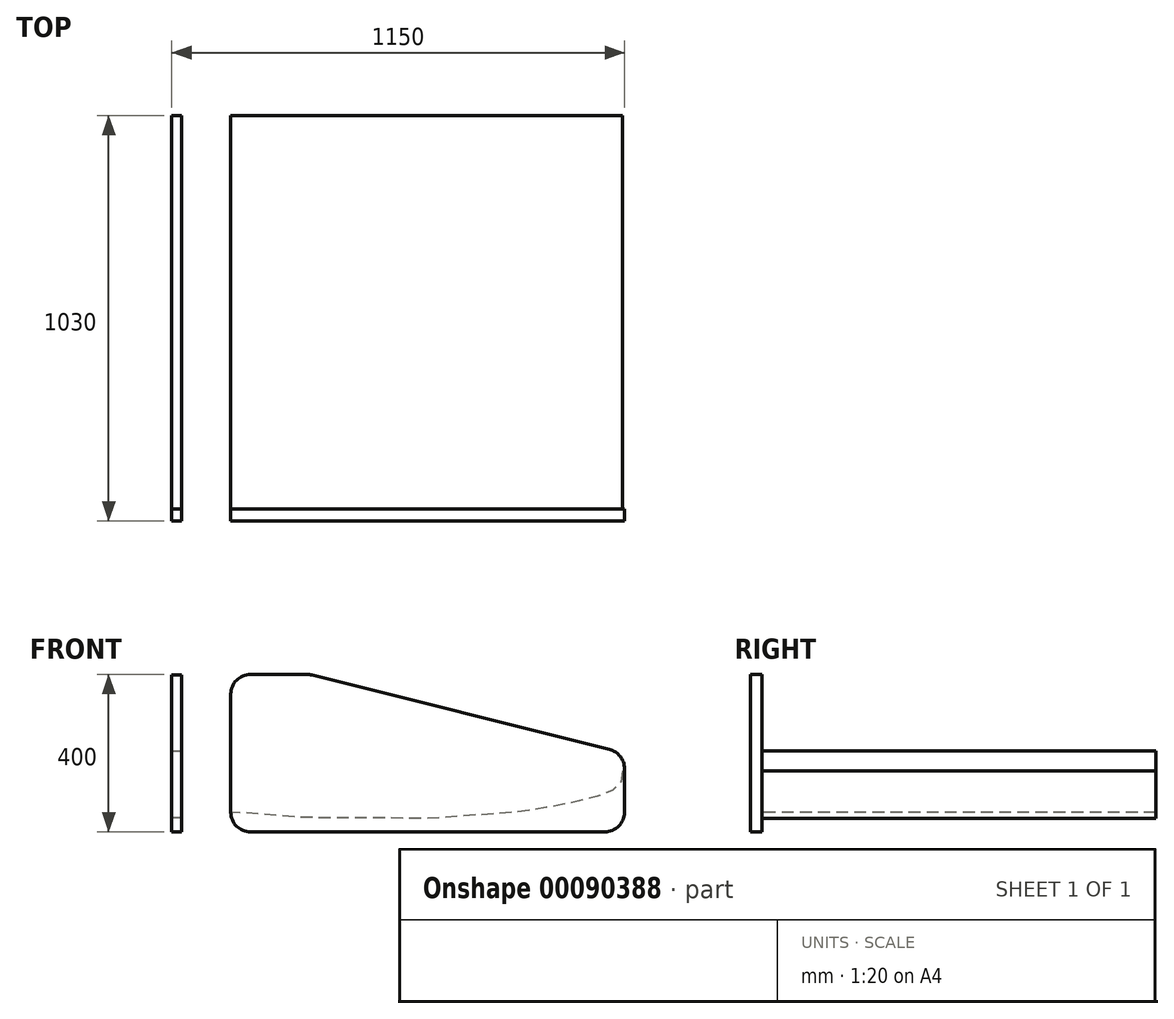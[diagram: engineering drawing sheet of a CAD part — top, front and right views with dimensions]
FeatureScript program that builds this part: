
annotation { "Feature Type Name" : "Feature", "Feature Type Description" : "" }
export const myFeature = defineFeature(function(context is Context, id is Id, definition is map)
    precondition{}
    {
        {
            var Q0;
            Q0=qCreatedBy(makeId("Front.planeOp"),FACE);
            var sketch = newSketch(context, id + "F0", { "sketchPlane" : qUnion([Q0])});
            skFitSpline(sketch, "E0", {"points": [v(500, -115.65) * mm, v(486.98, -151.94) * mm, v(400.8, -177.57) * mm, v(301.65, -187.35) * mm, v(199.93, -190.98) * mm, v(100.11, -187.23) * mm, v(-0.38, -183.55) * mm, v(-133.74, -168.4) * mm, v(-300.9, -150.5) * mm, v(-433.38, -126.44) * mm, v(-500, -115.65) * mm]});
            skFitSpline(sketch, "E1", {"points": [v(500, -115.65) * mm, v(486.98, -79.36) * mm, v(400.8, -53.72) * mm, v(301.65, -43.94) * mm, v(199.93, -40.32) * mm, v(100.11, -44.06) * mm, v(-0.38, -47.75) * mm, v(-133.74, -62.9) * mm, v(-300.9, -80.8) * mm, v(-433.38, -104.86) * mm, v(-500, -115.65) * mm]});
            skLineSegment(sketch, "E2", {"start": v(-500, -115.65) * mm, "end": v(0, 0) * mm, "construction": true});
            skSolve(sketch);
        }
        {
            var Q0;
            Q0 = qSketchRegion(id + "F0", true);
            extrude(context, id + "F1", {"entities" : qUnion([Q0]), "oppositeDirection" : true, "depth" : 1000 * mm});
        }
        {
            var Q0;
            Q0=makeQuery(id+"F1.opExtrude","SWEPT_BODY",BODY,{"disambiguationData":[OSD([sQuery(id+"F0.wireOp",EDGE,"E0"),sQuery(id+"F0.wireOp",EDGE,"E1")])]});
            var Q1;
            Q1=sQuery(id+"F0.wireOp",EDGE,"E2");
            transform(context, id + "F2", {"entities" : qUnion([Q0]), "transformType" : TransformType.TRANSLATION_ENTITY, "oppositeDirectionEntity" : false, "transformLine" : qUnion([Q1]), "makeCopy" : false});
        }
        {
            var Q0;
            Q0=makeQuery(id+"F1.opExtrude","SWEPT_BODY",BODY,{"disambiguationData":[OSD([sQuery(id+"F0.wireOp",EDGE,"E0"),sQuery(id+"F0.wireOp",EDGE,"E1")])]});
            var Q1;
            {var subQ0=sQuery(id+"F0.wireOp",EDGE,"E1");var subQ1=sQuery(id+"F0.wireOp",EDGE,"E0");Q1=makeQuery(id+"F1.opExtrude","SWEPT_EDGE",EDGE,{"disambiguationData":[OSD([subQ1,subQ0]),TDD([makeQuery(id+"F0.imprint","INTERSECT",VERTEX,{"disambiguationData":[OD(1.0)],"derivedFrom":[subQ1,subQ0]})])]});}
            transform(context, id + "F3", {"entities" : qUnion([Q0]), "transformType" : TransformType.ROTATION, "transformAxis" : qUnion([Q1]), "angle" : 6 * degree, "makeCopy" : false});
        }
        {
            var Q0;
            Q0=qCreatedBy(makeId("Front.planeOp"),FACE);
            var sketch = newSketch(context, id + "F4", { "sketchPlane" : qUnion([Q0])});
            skLineSegment(sketch, "E3", {"start": v(0, -50) * mm, "end": v(0, 350) * mm});
            skLineSegment(sketch, "E4", {"start": v(0, 350) * mm, "end": v(200, 350) * mm});
            skLineSegment(sketch, "E5", {"start": v(200, 350) * mm, "end": v(1000, 150) * mm});
            skLineSegment(sketch, "E6", {"start": v(1000, 150) * mm, "end": v(1000, -50) * mm});
            skLineSegment(sketch, "E7", {"start": v(1000, -50) * mm, "end": v(0, -50) * mm});
            skSolve(sketch);
        }
        {
            var Q0;
            Q0 = qSketchRegion(id + "F4", true);
            extrude(context, id + "F5", {"entities" : qUnion([Q0]), "operationType" : NewBodyOperationType.ADD, "depth" : 30 * mm});
        }
        {
            var Q0;
            Q0=makeQuery(id+"F5.opExtrude","SWEPT_EDGE",EDGE,{"disambiguationData":[OSD([sQuery(id+"F4.wireOp",EDGE,"E3"),sQuery(id+"F4.wireOp",EDGE,"E4")])]});
            var Q1;
            Q1=makeQuery(id+"F5.opExtrude","SWEPT_EDGE",EDGE,{"disambiguationData":[OSD([sQuery(id+"F4.wireOp",EDGE,"E4"),sQuery(id+"F4.wireOp",EDGE,"E5")])]});
            var Q2;
            Q2=makeQuery(id+"F5.opExtrude","SWEPT_EDGE",EDGE,{"disambiguationData":[OSD([sQuery(id+"F4.wireOp",EDGE,"E5"),sQuery(id+"F4.wireOp",EDGE,"E6")])]});
            var Q3;
            Q3=makeQuery(id+"F5.opExtrude","SWEPT_EDGE",EDGE,{"disambiguationData":[OSD([sQuery(id+"F4.wireOp",EDGE,"E6"),sQuery(id+"F4.wireOp",EDGE,"E7")])]});
            var Q4;
            Q4=makeQuery(id+"F5.opExtrude","SWEPT_EDGE",EDGE,{"disambiguationData":[OSD([sQuery(id+"F4.wireOp",EDGE,"E3"),sQuery(id+"F4.wireOp",EDGE,"E7")])]});
            fillet(context, id + "F6", {"entities" : qUnion([Q0, Q1, Q2, Q3, Q4]), "radius" : 50 * mm, "tangentPropagation" : true, "allowEdgeOverflow" : false});
        }
        {
            var Q0;
            Q0=qCreatedBy(makeId("Right.planeOp"),FACE);
            cPlane(context, id + "F7", {"entities" : qUnion([Q0]), "cplaneType" : CPlaneType.OFFSET, "offset" : 150 * mm, "oppositeDirection" : true, "width" : 150 * mm, "height" : 150 * mm});
        }
        {
            var Q0;
            Q0=qCreatedBy(id+"F7.planeOp",FACE);
            var sketch = newSketch(context, id + "F8", { "sketchPlane" : qUnion([Q0])});
            skLineSegment(sketch, "E8.0", {"start": v(-30, 348.5) * mm, "end": v(-30, 159.47) * mm});
            skLineSegment(sketch, "E9.0", {"start": v(0, 348.5) * mm, "end": v(-30, 348.5) * mm});
            skLineSegment(sketch, "E10.0", {"start": v(0, 348.5) * mm, "end": v(0, 159.47) * mm});
            skLineSegment(sketch, "E11", {"start": v(0, 154.88) * mm, "end": v(1000, 154.88) * mm});
            skLineSegment(sketch, "E12.0", {"start": v(-30, 110.96) * mm, "end": v(-30, 159.47) * mm});
            skLineSegment(sketch, "E13.0", {"start": v(-30, 110.96) * mm, "end": v(-30, 0) * mm});
            skLineSegment(sketch, "E14.0", {"start": v(-30, -50) * mm, "end": v(-30, 0) * mm});
            skLineSegment(sketch, "E15.0", {"start": v(0, -14.74) * mm, "end": v(0, -50) * mm});
            skLineSegment(sketch, "E16", {"start": v(1000, -14.74) * mm, "end": v(0, -14.74) * mm});
            skLineSegment(sketch, "E17", {"start": v(1000, 154.88) * mm, "end": v(1000, -14.74) * mm});
            skLineSegment(sketch, "E18", {"start": v(0, -50) * mm, "end": v(-30, -50) * mm});
            skLineSegment(sketch, "E19", {"start": v(0, 159.47) * mm, "end": v(0, 154.88) * mm});
            skPoint(sketch, "E20.orphan", {"position": v(0, 0) * mm});
            skSolve(sketch);
        }
        {
            var Q0;
            Q0 = qSketchRegion(id + "F8", true);
            extrude(context, id + "F9", {"entities" : qUnion([Q0]), "depth" : 25 * mm});
        }
    });
